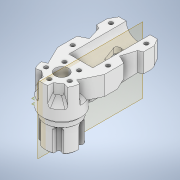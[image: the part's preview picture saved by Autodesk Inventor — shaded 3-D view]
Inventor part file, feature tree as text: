
AUTODESK INVENTOR PART (.ipt)
format: ipt  version: 2020 (Build 240168000, 168)  size: 913,408 bytes
history: native  units: mm
features: projected_geometry x21, extrude x17, sketch x17, chamfer x8, other x7, fillet x6, thicken_offset x5, reference x5, draft x4, plane x3, mirror x3, pattern_circular x2, hole x1
ambient origin geometry x8: Origin, YZ Plane, XZ Plane, XY Plane, X Axis, Y Axis, Z Axis, Center Point
bodies: Solid1 (feature_tree)
feature tree (99):
  extrude  "Extrusion1"  Depth=12.0mm
  extrude  "Extrusion2"  Depth=18.0mm
  extrude  "Extrusion3"  Depth=20.0mm
  extrude  "Extrusion4"  Depth=60.0mm TaperAngle=0.0deg
  extrude  "Extrusion5"  Depth=45.0mm TaperAngle=0.0deg
  plane  "Work Plane1"
  extrude  "Extrusion6"  Depth=8.0mm
  pattern_circular  "Circular Pattern1"  Count=9  [1 undecoded]
  thicken_offset  "Thicken1"
  extrude  "Extrusion7"  Depth=2.0mm
  extrude  "Extrusion8"  Depth=90.0mm TaperAngle=0.0deg
  extrude  "Extrusion9"  Depth=50.0mm
  thicken_offset  "Thicken2"
  thicken_offset  "Thicken3"
  extrude  "Extrusion10"  Depth=4.2mm
  extrude  "Extrusion11"  Depth=125.0mm
  mirror  "Mirror1"
  thicken_offset  "Thicken4"
  thicken_offset  "Thicken5"
  extrude  "Extrusion12"  Depth=2.0mm
  extrude  "Extrusion16"  Depth=2.0mm
  mirror  "Mirror2"
  chamfer  "Chamfer1"  Distance=2.0mm
  hole  "Hole1"  [1 undecoded]
  chamfer  "Chamfer2"  Distance=40.0mm
  chamfer  "Chamfer3"  Distance=4.2mm
  fillet  "Fillet3"  Radius=4.2mm
  plane  "Work Plane3"
  extrude  "Extrusion18"  Depth=2.0mm TaperAngle=0.0deg
  extrude  "Extrusion19"  Depth=2.0mm
  mirror  "Mirror3"
  plane  "Work Plane4"
  extrude  "Extrusion20"  TaperAngle=30.0deg  [1 undecoded]
  pattern_circular  "Circular Pattern3"  Count=6 Angle=360.0deg
  chamfer  "Chamfer6"  Distance=4.2mm
  fillet  "Fillet6"  [1 undecoded]
  fillet  "Fillet7"  Radius=60.0mm
  chamfer  "Chamfer7"  Distance=4.0mm
  chamfer  "Chamfer8"  Distance=2.0mm
  extrude  "Extrusion21"  Depth=2.0mm
  draft  "FaceDraft1"
  draft  "FaceDraft2"
  draft  "FaceDraft3"
  draft  "FaceDraft4"
  chamfer  "Chamfer9"  Distance=2.0mm
  fillet  "Fillet10"  Radius=2.0mm
  fillet  "Fillet11"  Radius=15.0mm
  fillet  "Fillet12"  Radius=8.0mm
  chamfer  "Chamfer10"  Distance=8.0mm
  sketch  "Sketch1"  dims[d0=12.0mm d1=12.0mm]
  reference  "Reference1"
  sketch  "Sketch2"  dims[d2=18.0mm d3=18.0mm]
  projected_geometry  "Projected Loop1"
  sketch  "Sketch3"  dims[d4=60.0mm d5=0.0mm d6=20.0mm]
  projected_geometry  "Projected Loop2"
  sketch  "Sketch4"  dims[d7=40.0mm d8=60.0mm d9=0.0mm]
  projected_geometry  "Projected Loop3"
  projected_geometry  "Projected Loop4"
  sketch  "Sketch5"  dims[d10=40.0mm d11=45.0mm d12=0.0mm]
  projected_geometry  "Projected Loop5"
  projected_geometry  "Projected Loop6"
  sketch  "Sketch7"  dims[d13=45.0mm d14=0.0mm d15=8.0mm]
  projected_geometry  "Projected Loop10"
  sketch  "Sketch8"  dims[d16=8.0mm]
  projected_geometry  "Projected Loop11"
  sketch  "Sketch9"  dims[d17=45.0mm d18=0.0mm]
  projected_geometry  "Projected Loop12"
  sketch  "Sketch10"  dims[d23=13.0mm]
  projected_geometry  "Projected Loop13"
  projected_geometry  "Projected Loop14"
  projected_geometry  "Projected Loop15"
  projected_geometry  "Projected Loop16"
  projected_geometry  "Projected Loop17"
  projected_geometry  "Projected Loop18"
  sketch  "Sketch12"  dims[d24=4.2mm d25=90.0mm d26=0.0mm]
  projected_geometry  "Projected Loop19"
  sketch  "Sketch14"  dims[d27=50.0mm d28=360.0deg d30=2.0mm d31=4.0mm]
  projected_geometry  "Projected Loop22"
  sketch  "Sketch18"  dims[d32=14.0mm d33=90.0mm d34=0.0mm]
  projected_geometry  "Projected Loop27"
  sketch  "Sketch20"  dims[d35=50.0mm d36=50.0mm]
  projected_geometry  "Projected Loop29"
  reference  "Reference2"
  sketch  "Sketch21"  dims[d37=4.2mm d38=4.2mm]
  projected_geometry  "Projected Loop30"
  sketch  "Sketch22"  dims[d39=90.0mm d40=0.0mm d41=125.0mm]
  projected_geometry  "Projected Loop31"
  sketch  "Sketch23"  dims[d42=90.0mm d43=0.0mm d44=2.0mm]
  sketch  "Sketch24"  dims[d45=2.0mm d46=2.0mm d47=2.0mm d48=40.0mm d49=40.0mm d50=4.2mm d51=4.2mm d52=90.0mm d53=0.0mm d54=4.2mm d56=30.0deg d57=60.0mm d59=360.0deg d61=4.2mm d62=30.0deg d63=60.0mm d65=360.0deg d67=4.0mm d68=0.0mm d69=2.0mm d70=2.0mm d71=2.0mm d72=2.0mm d82=15.0mm d83=8.0mm d84=8.0mm d85=4.0mm d86=2.0mm d87=20.0mm d88=0.0mm d103=22.68928mm d104=15.0mm d105=17.453293mm d106=20.0mm d107=0.0mm d111=6.0mm d112=2.0mm d113=45.0deg d114=4.2mm d115=6.0mm d116=4.0mm d117=2.0mm d118=90.0deg d119=5.0mm d120=0.0mm d121=4.5mm d122=2.0mm d123=60.0deg d124=4.5mm d125=2.0mm d126=60.0deg d128=2.0mm d146=13.5mm d147=35.0mm d148=150.0mm d149=40.0mm d150=0.0mm d151=5.0mm d152=4.0mm d153=13.5mm d154=40.0mm d155=0.0mm d156=5.0mm d158=15.0deg d159=15.0deg d160=34.0mm d161=40.0mm d162=0.0mm d163=50.0mm d164=360.0deg d166=0.5mm d167=2.0mm d168=45.0deg d169=2.0mm d170=3.0mm d171=1.0mm d172=2.0mm d173=45.0deg d174=2.0mm d175=2.0mm d176=45.0deg d177=40.0mm d178=0.0mm d187=60.0deg d188=60.0deg d189=60.0deg d190=60.0deg d192=2.5mm d193=2.0mm d194=60.0deg d196=3.0mm d197=3.0mm d198=2.0mm d201=3.0mm d202=2.0mm d203=45.0deg d101=0.5mm d102=0.872665mm]
  reference  "Reference3"
  reference  "Reference4"
  reference  "Reference5"
  parser-record x2  (decoder bookkeeping rows leaked as tree rows — omitted from the tree; the rows remain in map.json)
  other  "sub_leg_1.iam"
  other  "carbon_fiber_25_21_300:1"
  other  "joint_connector_6:1"
  other  "sub_leg_1_lit.iam"
  other  "joint_connector_5_lit:1"
note: 4 required parameter values undecoded (feature->parameter linkage not recoverable at this tier; creation-order binding heuristic only, values carry confidence <= 0.55)
note: 2 file-system paths scrubbed to <path> (originals preserved in map.json)
